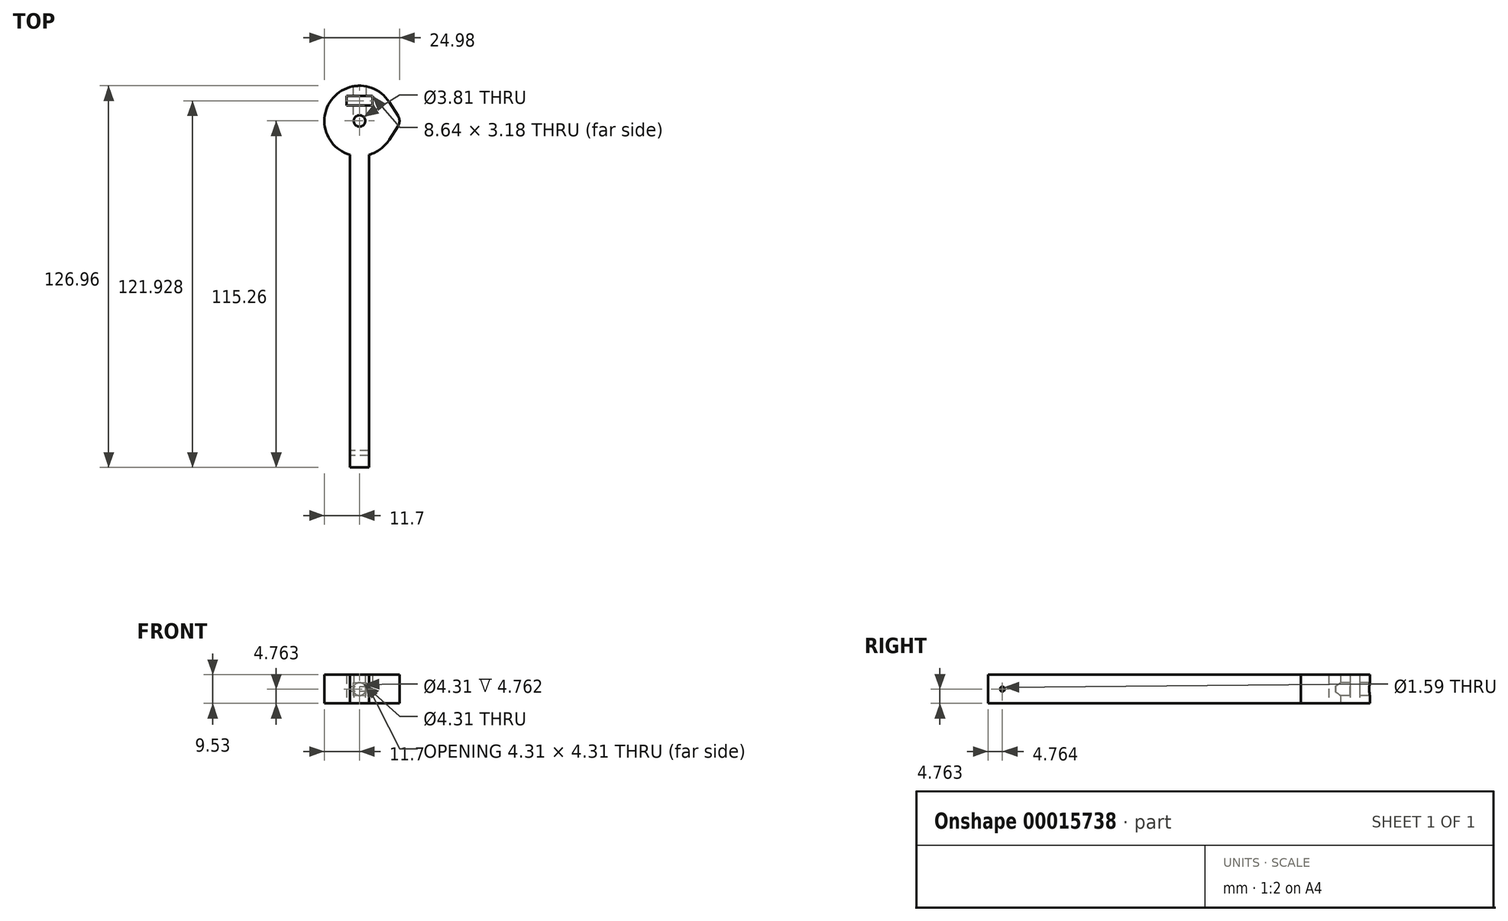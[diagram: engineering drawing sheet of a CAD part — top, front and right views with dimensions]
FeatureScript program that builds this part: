
annotation { "Feature Type Name" : "Feature", "Feature Type Description" : "" }
export const myFeature = defineFeature(function(context is Context, id is Id, definition is map)
    precondition{}
    {
        {
            var Q0;
            Q0=qCreatedBy(makeId("Top.planeOp"),FACE);
            var sketch = newSketch(context, id + "F0", { "sketchPlane" : qUnion([Q0])});
            skCircle(sketch, "E0", {"center": v(0, 0) * mm, "radius": 1.9 * mm});
            skLineSegment(sketch, "E1", {"start": v(0, 0) * mm, "end": v(0, 1.9) * mm, "construction": true});
            skLineSegment(sketch, "E2", {"start": v(0, 1.9) * mm, "end": v(0, 5.08) * mm, "construction": true});
            skLineSegment(sketch, "E3.bottom", {"start": v(-4.32, 5.08) * mm, "end": v(4.32, 5.08) * mm});
            skLineSegment(sketch, "E3.top", {"start": v(-4.32, 8.26) * mm, "end": v(4.32, 8.26) * mm});
            skLineSegment(sketch, "E3.left", {"start": v(-4.32, 5.08) * mm, "end": v(-4.32, 8.26) * mm});
            skLineSegment(sketch, "E3.right", {"start": v(4.32, 5.08) * mm, "end": v(4.32, 8.26) * mm});
            skArc(sketch, "E4", {"start": v(3.17, -11.26) * mm, "mid": v(0, 11.7) * mm, "end": v(-3.18, -11.26) * mm});
            skCircle(sketch, "E5", {"center": v(4.32, 8.26) * mm, "radius": 2.38 * mm, "construction": true});
            skLineSegment(sketch, "E6.bottom", {"start": v(-3.17, -11.26) * mm, "end": v(3.17, -11.26) * mm, "construction": true});
            skLineSegment(sketch, "E6.top", {"start": v(-3.17, -115.26) * mm, "end": v(3.17, -115.26) * mm});
            skLineSegment(sketch, "E6.left", {"start": v(-3.17, -11.26) * mm, "end": v(-3.17, -115.26) * mm});
            skLineSegment(sketch, "E6.right", {"start": v(3.18, -11.26) * mm, "end": v(3.18, -115.26) * mm});
            skLineSegment(sketch, "E7", {"start": v(0, 0) * mm, "end": v(0, -11.26) * mm, "construction": true});
            skSolve(sketch);
        }
        {
            var Q0;
            Q0 = qSketchRegion(id + "F0", true);
            extrude(context, id + "F1", {"entities" : qUnion([Q0]), "depth" : 9.52 * mm});
        }
        {
            var Q0;
            Q0=makeQuery(id+"F1.opExtrude","SWEPT_FACE",FACE,{"disambiguationData":[OSD([sQuery(id+"F0.wireOp",EDGE,"E3.bottom")])]});
            var sketch = newSketch(context, id + "F2", { "sketchPlane" : qUnion([Q0])});
            skLineSegment(sketch, "E8", {"start": v(0, 9.53) * mm, "end": v(0, 0) * mm, "construction": true});
            skCircle(sketch, "E9", {"center": v(0, 4.76) * mm, "radius": 2.15 * mm});
            skSolve(sketch);
        }
        {
            var Q0;
            Q0 = qSketchRegion(id + "F2", true);
            var Q1;
            Q1=makeQuery(id+"F1.opExtrude","SWEPT_FACE",FACE,{"disambiguationData":[OSD([sQuery(id+"F0.wireOp",EDGE,"E4")])]});
            var Q2;
            Q2=makeQuery(id+"F1.opExtrude","SWEPT_FACE",FACE,{"disambiguationData":[OSD([sQuery(id+"F0.wireOp",EDGE,"E0")])]});
            extrude(context, id + "F3", {"entities" : qUnion([Q0]), "operationType" : NewBodyOperationType.REMOVE, "endBound" : BoundingType.UP_TO_SURFACE, "endBoundEntityFace" : qUnion([Q1]), "depth" : 25.4 * mm, "hasSecondDirection" : true, "secondDirectionOppositeDirection" : true, "secondDirectionBoundEntityFace" : qUnion([Q2]), "secondDirectionDepth" : 4.76 * mm});
        }
        {
            var Q0;
            Q0=makeQuery(id+"F1.opExtrude","CAP_FACE",FACE,{"disambiguationData":[OSD([sQuery(id+"F0.wireOp",EDGE,"E0"),sQuery(id+"F0.wireOp",EDGE,"E3.bottom"),sQuery(id+"F0.wireOp",EDGE,"E3.top"),sQuery(id+"F0.wireOp",EDGE,"E3.left"),sQuery(id+"F0.wireOp",EDGE,"E3.right"),sQuery(id+"F0.wireOp",EDGE,"E4"),sQuery(id+"F0.wireOp",EDGE,"E6.top"),sQuery(id+"F0.wireOp",EDGE,"E6.left"),sQuery(id+"F0.wireOp",EDGE,"E6.right")])],"isStart":true});
            var sketch = newSketch(context, id + "F4", { "sketchPlane" : qUnion([Q0])});
            skLineSegment(sketch, "E10", {"start": v(0, 0) * mm, "end": v(11.7, 0) * mm, "construction": true});
            skLineSegment(sketch, "E11", {"start": v(11.7, 0) * mm, "end": v(13.28, 0) * mm, "construction": true});
            skArc(sketch, "E12", {"start": v(12.79, -1.7) * mm, "mid": v(13.28, 0) * mm, "end": v(12.79, 1.7) * mm});
            skLineSegment(sketch, "E13", {"start": v(12.79, 1.7) * mm, "end": v(9.86, 6.3) * mm});
            skLineSegment(sketch, "E14", {"start": v(12.79, -1.7) * mm, "end": v(9.86, -6.3) * mm});
            skArc(sketch, "E15", {"start": v(9.86, -6.3) * mm, "mid": v(11.7, 0) * mm, "end": v(9.86, 6.3) * mm});
            skSolve(sketch);
        }
        {
            var Q0;
            Q0 = qSketchRegion(id + "F4", true);
            var Q1;
            Q1=makeQuery(id+"F1.opExtrude","CAP_FACE",FACE,{"disambiguationData":[OSD([sQuery(id+"F0.wireOp",EDGE,"E0"),sQuery(id+"F0.wireOp",EDGE,"E3.bottom"),sQuery(id+"F0.wireOp",EDGE,"E3.top"),sQuery(id+"F0.wireOp",EDGE,"E3.left"),sQuery(id+"F0.wireOp",EDGE,"E3.right"),sQuery(id+"F0.wireOp",EDGE,"E4"),sQuery(id+"F0.wireOp",EDGE,"E6.top"),sQuery(id+"F0.wireOp",EDGE,"E6.left"),sQuery(id+"F0.wireOp",EDGE,"E6.right")])],"isStart":false});
            extrude(context, id + "F5", {"entities" : qUnion([Q0]), "operationType" : NewBodyOperationType.ADD, "endBound" : BoundingType.UP_TO_SURFACE, "oppositeDirection" : true, "endBoundEntityFace" : qUnion([Q1]), "depth" : 25.4 * mm});
        }
        {
            var Q0;
            Q0=makeQuery(id+"F1.opExtrude","SWEPT_FACE",FACE,{"disambiguationData":[OSD([sQuery(id+"F0.wireOp",EDGE,"E6.left")])]});
            var sketch = newSketch(context, id + "F6", { "sketchPlane" : qUnion([Q0])});
            skLineSegment(sketch, "E16.bottom", {"start": v(115.26, 4.76) * mm, "end": v(110.5, 4.76) * mm, "construction": true});
            skLineSegment(sketch, "E16.top", {"start": v(115.26, 0) * mm, "end": v(110.5, 0) * mm, "construction": true});
            skLineSegment(sketch, "E16.left", {"start": v(115.26, 4.76) * mm, "end": v(115.26, 0) * mm, "construction": true});
            skLineSegment(sketch, "E16.right", {"start": v(110.5, 4.76) * mm, "end": v(110.5, 0) * mm, "construction": true});
            skCircle(sketch, "E17", {"center": v(110.5, 4.76) * mm, "radius": 0.8 * mm});
            skSolve(sketch);
        }
        {
            var Q0;
            Q0 = qSketchRegion(id + "F6", true);
            var Q1;
            Q1=makeQuery(id+"F1.opExtrude","SWEPT_FACE",FACE,{"disambiguationData":[OSD([sQuery(id+"F0.wireOp",EDGE,"E6.right")])]});
            extrude(context, id + "F7", {"entities" : qUnion([Q0]), "operationType" : NewBodyOperationType.REMOVE, "endBound" : BoundingType.UP_TO_SURFACE, "oppositeDirection" : true, "endBoundEntityFace" : qUnion([Q1]), "depth" : 25.4 * mm});
        }
    });
